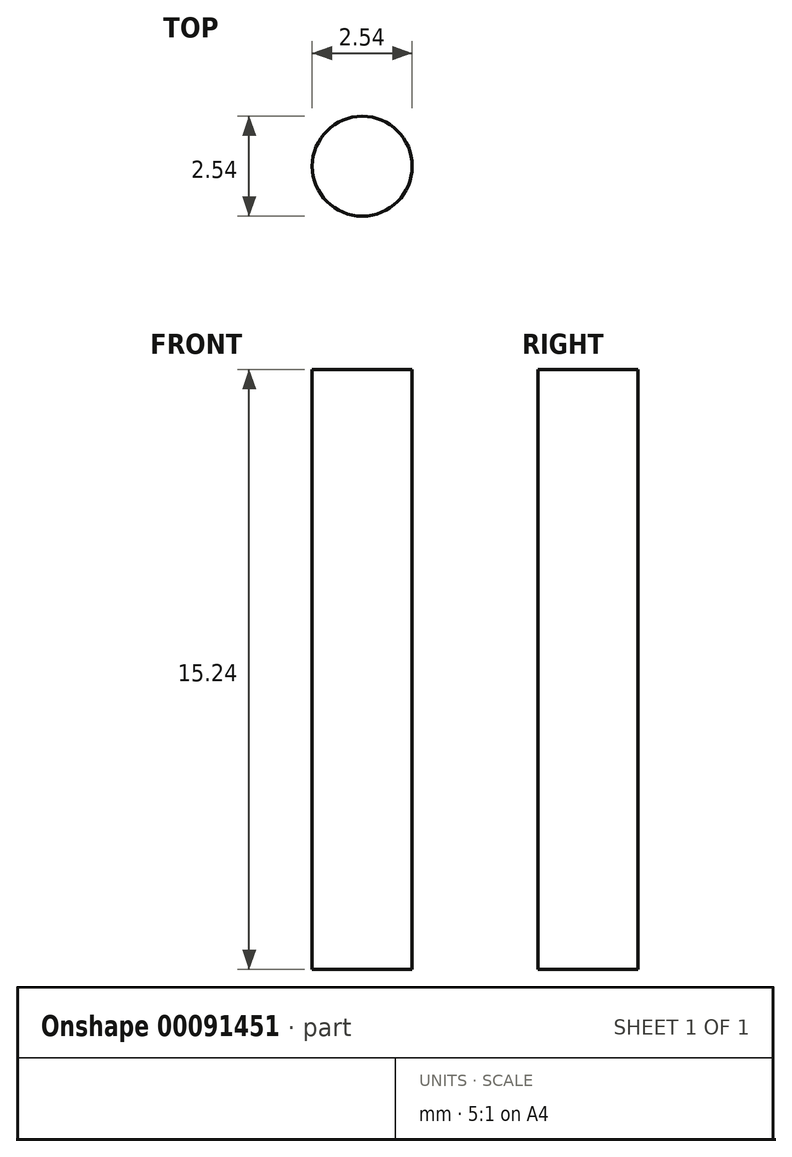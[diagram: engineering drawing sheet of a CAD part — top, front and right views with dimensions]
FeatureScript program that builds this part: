
annotation { "Feature Type Name" : "Feature", "Feature Type Description" : "" }
export const myFeature = defineFeature(function(context is Context, id is Id, definition is map)
    precondition{}
    {
        {
            var Q0;
            Q0=qCreatedBy(makeId("Top.planeOp"),FACE);
            var sketch = newSketch(context, id + "F0", { "sketchPlane" : qUnion([Q0])});
            skCircle(sketch, "E0", {"center": v(-47.63, -1.71) * mm, "radius": 1.27 * mm});
            skSolve(sketch);
        }
        {
            var Q0;
            Q0=makeQuery(id+"F0.imprint","IMPRINT",FACE,{"disambiguationData":[TD([[makeQuery(id+"F0.imprint","IMPRINT",EDGE,{"derivedFrom":sQuery(id+"F0.wireOp",EDGE,"E0")}),1.0]])]});
            extrude(context, id + "F1", {"entities" : qUnion([Q0]), "depth" : 15.24 * mm});
        }
    });
